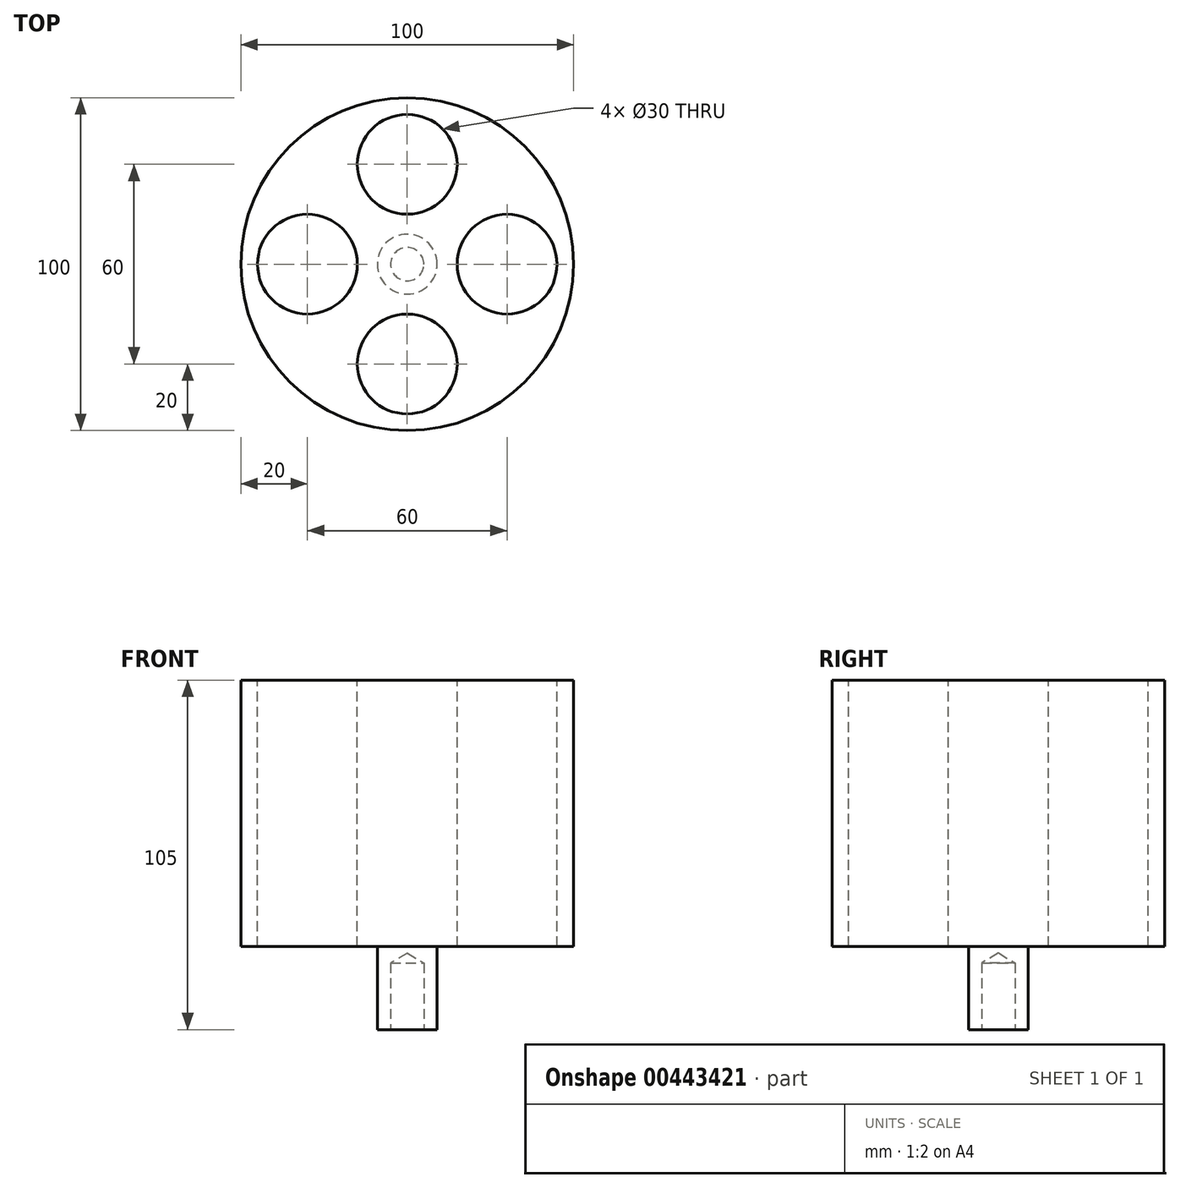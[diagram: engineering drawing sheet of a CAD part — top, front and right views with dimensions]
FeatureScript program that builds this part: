
annotation { "Feature Type Name" : "Feature", "Feature Type Description" : "" }
export const myFeature = defineFeature(function(context is Context, id is Id, definition is map)
    precondition{}
    {
        {
            var Q0;
            Q0=qCreatedBy(makeId("Top.planeOp"),FACE);
            var sketch = newSketch(context, id + "F0", { "sketchPlane" : qUnion([Q0])});
            skCircle(sketch, "E0", {"center": v(0, 0) * mm, "radius": 50 * mm});
            skSolve(sketch);
        }
        {
            var Q0;
            Q0=makeQuery(id+"F0.imprint","IMPRINT",FACE,{"disambiguationData":[TD([[makeQuery(id+"F0.imprint","IMPRINT",EDGE,{"derivedFrom":sQuery(id+"F0.wireOp",EDGE,"E0")}),1.0]])]});
            extrude(context, id + "F1", {"entities" : qUnion([Q0]), "depth" : 80 * mm});
        }
        {
            var Q0;
            Q0=makeQuery(id+"F1.opExtrude","CAP_FACE",FACE,{"disambiguationData":[OSD([sQuery(id+"F0.wireOp",EDGE,"E0")])],"isStart":false});
            var sketch = newSketch(context, id + "F2", { "sketchPlane" : qUnion([Q0])});
            skCircle(sketch, "E1", {"center": v(0, 0) * mm, "radius": 30 * mm, "construction": true});
            skCircle(sketch, "E2", {"center": v(0, 30) * mm, "radius": 15 * mm});
            skCircle(sketch, "E3.1.0", {"center": v(-30, 0) * mm, "radius": 15 * mm});
            skCircle(sketch, "E3.2.0", {"center": v(0, -30) * mm, "radius": 15 * mm});
            skCircle(sketch, "E3.3.0", {"center": v(30, 0) * mm, "radius": 15 * mm});
            skSolve(sketch);
        }
        {
            var Q0;
            Q0=makeQuery(id+"F2.imprint","IMPRINT",FACE,{"disambiguationData":[TD([[makeQuery(id+"F2.imprint","IMPRINT",EDGE,{"derivedFrom":sQuery(id+"F2.wireOp",EDGE,"E2")}),1.0]])]});
            var Q1;
            Q1=makeQuery(id+"F2.imprint","IMPRINT",FACE,{"disambiguationData":[TD([[makeQuery(id+"F2.imprint","IMPRINT",EDGE,{"derivedFrom":sQuery(id+"F2.wireOp",EDGE,"E3.1.0")}),1.0]])]});
            var Q2;
            Q2=makeQuery(id+"F2.imprint","IMPRINT",FACE,{"disambiguationData":[TD([[makeQuery(id+"F2.imprint","IMPRINT",EDGE,{"derivedFrom":sQuery(id+"F2.wireOp",EDGE,"E3.2.0")}),1.0]])]});
            var Q3;
            Q3=makeQuery(id+"F2.imprint","IMPRINT",FACE,{"disambiguationData":[TD([[makeQuery(id+"F2.imprint","IMPRINT",EDGE,{"derivedFrom":sQuery(id+"F2.wireOp",EDGE,"E3.3.0")}),1.0]])]});
            extrude(context, id + "F3", {"entities" : qUnion([Q0, Q1, Q2, Q3]), "operationType" : NewBodyOperationType.REMOVE, "endBound" : BoundingType.THROUGH_ALL, "oppositeDirection" : true, "depth" : 25 * mm});
        }
        {
            var Q0;
            Q0=makeQuery(id+"F1.opExtrude","CAP_FACE",FACE,{"disambiguationData":[OSD([sQuery(id+"F0.wireOp",EDGE,"E0")])],"isStart":true});
            var sketch = newSketch(context, id + "F4", { "sketchPlane" : qUnion([Q0])});
            skCircle(sketch, "E4", {"center": v(0, 0) * mm, "radius": 9 * mm});
            skSolve(sketch);
        }
        {
            var Q0;
            Q0=makeQuery(id+"F4.imprint","IMPRINT",FACE,{"disambiguationData":[TD([[makeQuery(id+"F4.imprint","IMPRINT",EDGE,{"derivedFrom":sQuery(id+"F4.wireOp",EDGE,"E4")}),1.0]])]});
            extrude(context, id + "F5", {"entities" : qUnion([Q0]), "operationType" : NewBodyOperationType.ADD, "depth" : 25 * mm});
        }
        {
            var Q0;
            Q0=makeQuery(id+"F5.opExtrude","CAP_FACE",FACE,{"disambiguationData":[OSD([sQuery(id+"F4.wireOp",EDGE,"E4")])],"isStart":false});
            var sketch = newSketch(context, id + "F6", { "sketchPlane" : qUnion([Q0])});
            skPoint(sketch, "E5", {"position": v(0, 0) * mm});
            skSolve(sketch);
        }
        {
            var Q0;
            Q0=sQuery(id+"F6.wireOp",VERTEX,"E5");
            var Q1;
            Q1=makeQuery(id+"F1.opExtrude","SWEPT_BODY",BODY,{"disambiguationData":[OSD([sQuery(id+"F0.wireOp",EDGE,"E0")])]});
            hole(context, id + "F7", {"style" : HoleStyle.SIMPLE, "endStyle" : HoleEndStyle.BLIND, "holeDiameter" : 10 * mm, "holeDepth" : 20 * mm, "isTappedThrough" : true, "tappedDepth" : 12 * mm, "tapClearance" : 3, "startFromSketch" : true, "locations" : qUnion([Q0]), "scope" : qUnion([Q1])});
        }
    });
